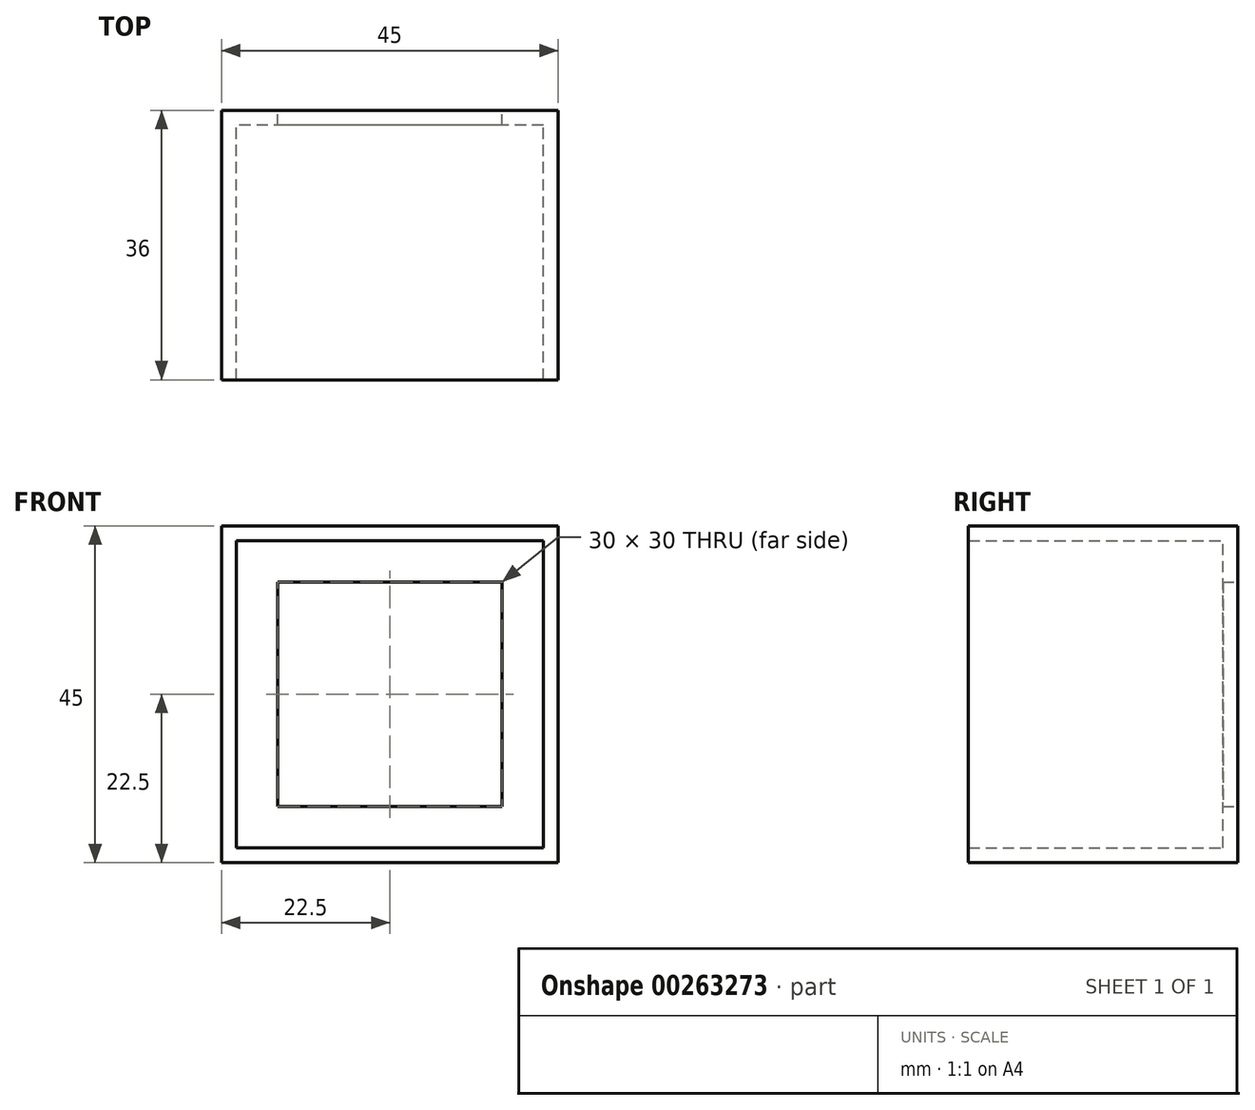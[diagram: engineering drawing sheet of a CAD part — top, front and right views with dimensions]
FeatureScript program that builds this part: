
annotation { "Feature Type Name" : "Feature", "Feature Type Description" : "" }
export const myFeature = defineFeature(function(context is Context, id is Id, definition is map)
    precondition{}
    {
        {
            var Q0;
            Q0=qCreatedBy(makeId("Front.planeOp"),FACE);
            var sketch = newSketch(context, id + "F0", { "sketchPlane" : qUnion([Q0])});
            skLineSegment(sketch, "E0.bottom", {"start": v(22.5, -22.5) * mm, "end": v(-22.5, -22.5) * mm});
            skLineSegment(sketch, "E0.top", {"start": v(22.5, 22.5) * mm, "end": v(-22.5, 22.5) * mm});
            skLineSegment(sketch, "E0.left", {"start": v(22.5, -22.5) * mm, "end": v(22.5, 22.5) * mm});
            skLineSegment(sketch, "E0.right", {"start": v(-22.5, -22.5) * mm, "end": v(-22.5, 22.5) * mm});
            skPoint(sketch, "E0.middle", {"position": v(0, 0) * mm});
            skSolve(sketch);
        }
        {
            var Q0;
            Q0 = qSketchRegion(id + "F0", true);
            extrude(context, id + "F1", {"entities" : qUnion([Q0]), "depth" : 36 * mm});
        }
        {
            var Q0;
            Q0=makeQuery(id+"F1.opExtrude","CAP_FACE",FACE,{"disambiguationData":[OSD([sQuery(id+"F0.wireOp",EDGE,"E0.bottom"),sQuery(id+"F0.wireOp",EDGE,"E0.top"),sQuery(id+"F0.wireOp",EDGE,"E0.left"),sQuery(id+"F0.wireOp",EDGE,"E0.right")])],"isStart":false});
            shell(context, id + "F2", {"entities" : qUnion([Q0]), "thickness" : 2 * mm});
        }
        {
            var Q0;
            Q0=makeQuery(id+"F1.opExtrude","CAP_FACE",FACE,{"disambiguationData":[OSD([sQuery(id+"F0.wireOp",EDGE,"E0.bottom"),sQuery(id+"F0.wireOp",EDGE,"E0.top"),sQuery(id+"F0.wireOp",EDGE,"E0.left"),sQuery(id+"F0.wireOp",EDGE,"E0.right")])],"isStart":true});
            var sketch = newSketch(context, id + "F3", { "sketchPlane" : qUnion([Q0])});
            skLineSegment(sketch, "E1.bottom", {"start": v(15, -15) * mm, "end": v(-15, -15) * mm});
            skLineSegment(sketch, "E1.top", {"start": v(15, 15) * mm, "end": v(-15, 15) * mm});
            skLineSegment(sketch, "E1.left", {"start": v(15, -15) * mm, "end": v(15, 15) * mm});
            skLineSegment(sketch, "E1.right", {"start": v(-15, -15) * mm, "end": v(-15, 15) * mm});
            skPoint(sketch, "E1.middle", {"position": v(0, 0) * mm});
            skSolve(sketch);
        }
        {
            var Q0;
            Q0 = qSketchRegion(id + "F3", true);
            extrude(context, id + "F4", {"entities" : qUnion([Q0]), "operationType" : NewBodyOperationType.REMOVE, "oppositeDirection" : true, "depth" : 25 * mm});
        }
    });
